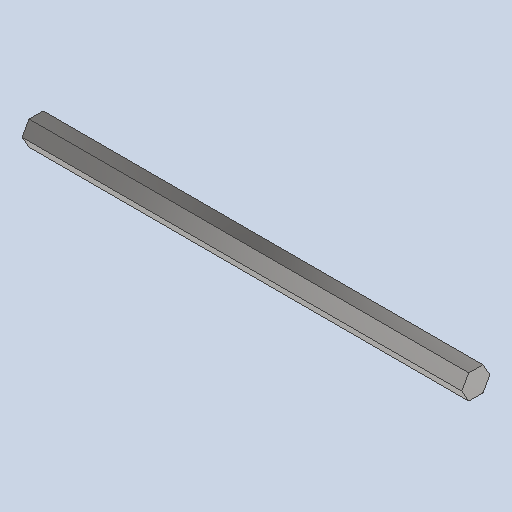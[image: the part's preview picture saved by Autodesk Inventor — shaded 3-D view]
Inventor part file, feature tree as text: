
AUTODESK INVENTOR PART (.ipt)
format: ipt  version: 2023 (Build 270158000, 158)  size: 89,600 bytes
history: native  units: in
note: dims shown in document units (in); Inventor stores cm internally (conversion verified against a paired STEP export)
features: other x3, sketch x1
ambient origin geometry x8: Origin, YZ Plane, XZ Plane, XY Plane, X Axis, Y Axis, Z Axis, Center Point
bodies: Solid1 (feature_tree)
feature tree (4):
  other  "9in-0.5inHexAxel.ipt"
  other  "Solid1::9in-0.5inHexAxel.ipt"
  other  "TaggingFeature1"
  sketch  "Sketch1"  dims[d0=0.3937in]
